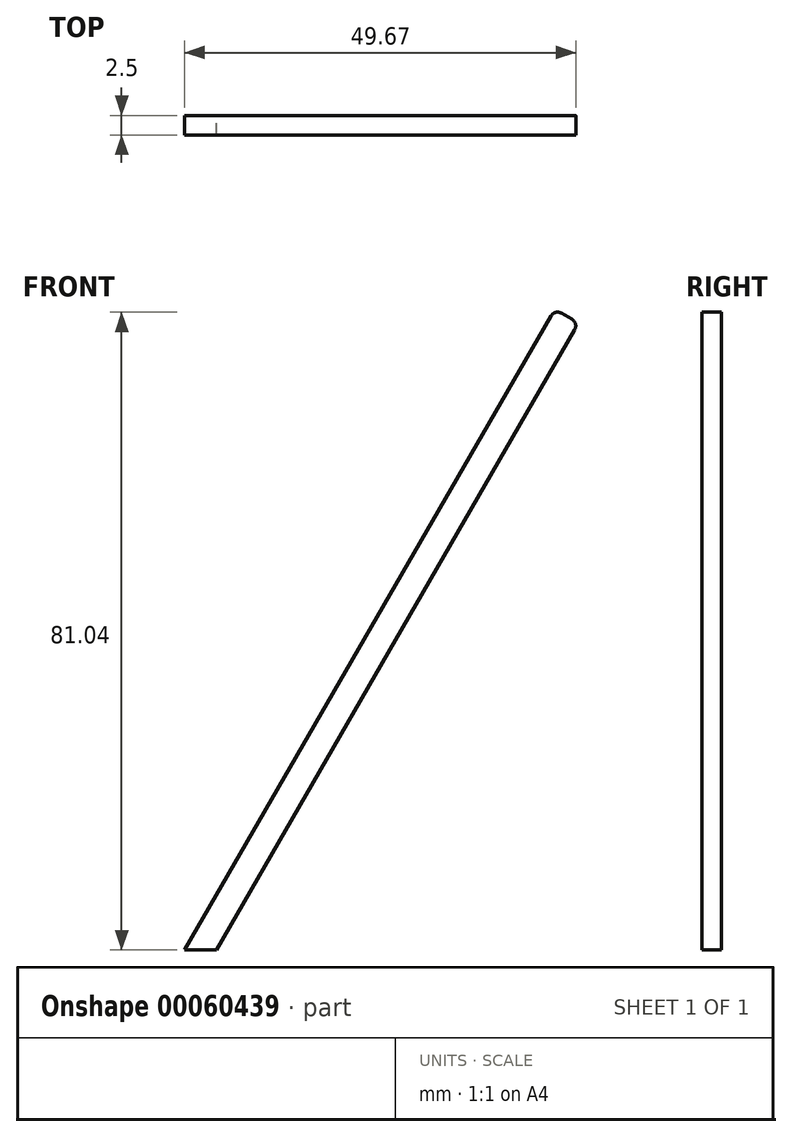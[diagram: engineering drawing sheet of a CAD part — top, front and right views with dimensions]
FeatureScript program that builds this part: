
annotation { "Feature Type Name" : "Feature", "Feature Type Description" : "" }
export const myFeature = defineFeature(function(context is Context, id is Id, definition is map)
    precondition{}
    {
        {
            var Q0;
            Q0=qCreatedBy(makeId("Front.planeOp"),FACE);
            var sketch = newSketch(context, id + "F0", { "sketchPlane" : qUnion([Q0])});
            skLineSegment(sketch, "E0.bottom", {"start": v(0, 0) * mm, "end": v(3.5, 0) * mm});
            skLineSegment(sketch, "E0.top", {"start": v(0, 94) * mm, "end": v(3.5, 94) * mm});
            skLineSegment(sketch, "E0.left", {"start": v(0, 0) * mm, "end": v(0, 94) * mm});
            skLineSegment(sketch, "E0.right", {"start": v(3.5, 0) * mm, "end": v(3.5, 94) * mm});
            skSolve(sketch);
        }
        {
            var Q0;
            Q0 = qSketchRegion(id + "F0", true);
            extrude(context, id + "F1", {"entities" : qUnion([Q0]), "depth" : 2.5 * mm});
        }
        {
            var Q0;
            Q0=makeQuery(id+"F1.opExtrude","SWEPT_EDGE",EDGE,{"disambiguationData":[OSD([sQuery(id+"F0.wireOp",EDGE,"E0.top"),sQuery(id+"F0.wireOp",EDGE,"E0.left")])]});
            var Q1;
            Q1=makeQuery(id+"F1.opExtrude","SWEPT_EDGE",EDGE,{"disambiguationData":[OSD([sQuery(id+"F0.wireOp",EDGE,"E0.top"),sQuery(id+"F0.wireOp",EDGE,"E0.right")])]});
            fillet(context, id + "F2", {"entities" : qUnion([Q0, Q1]), "radius" : 1 * mm, "allowEdgeOverflow" : false});
        }
        {
            var Q0;
            Q0=makeQuery(id+"F1.opExtrude","SWEPT_BODY",BODY,{"disambiguationData":[OSD([sQuery(id+"F0.wireOp",EDGE,"E0.bottom"),sQuery(id+"F0.wireOp",EDGE,"E0.top"),sQuery(id+"F0.wireOp",EDGE,"E0.left"),sQuery(id+"F0.wireOp",EDGE,"E0.right")])]});
            var Q1;
            Q1=makeQuery(id+"F1.opExtrude","SWEPT_EDGE",EDGE,{"disambiguationData":[OSD([sQuery(id+"F0.wireOp",EDGE,"E0.bottom"),sQuery(id+"F0.wireOp",EDGE,"E0.left")])]});
            transform(context, id + "F3", {"entities" : qUnion([Q0]), "transformType" : TransformType.ROTATION, "transformAxis" : qUnion([Q1]), "angle" : 30 * degree, "makeCopy" : false});
        }
        {
            var Q0;
            Q0=qCreatedBy(makeId("Front.planeOp"),FACE);
            var sketch = newSketch(context, id + "F4", { "sketchPlane" : qUnion([Q0])});
            skLineSegment(sketch, "E1.bottom", {"start": v(-30.77, 0) * mm, "end": v(32.26, 0) * mm});
            skLineSegment(sketch, "E1.top", {"start": v(-30.77, -8.78) * mm, "end": v(32.26, -8.78) * mm});
            skLineSegment(sketch, "E1.left", {"start": v(-30.77, 0) * mm, "end": v(-30.77, -8.78) * mm});
            skLineSegment(sketch, "E1.right", {"start": v(32.26, 0) * mm, "end": v(32.26, -8.78) * mm});
            skSolve(sketch);
        }
        {
            var Q0;
            Q0=makeQuery(id+"F4.imprint","IMPRINT",FACE,{"disambiguationData":[TD([[makeQuery(id+"F4.imprint","IMPRINT",EDGE,{"derivedFrom":sQuery(id+"F4.wireOp",EDGE,"E1.bottom")}),-1.0]])]});
            extrude(context, id + "F5", {"entities" : qUnion([Q0]), "depth" : 25 * mm});
        }
        {
            var Q0;
            Q0=makeQuery(id+"F5.opExtrude","SWEPT_BODY",BODY,{"disambiguationData":[OSD([sQuery(id+"F4.wireOp",EDGE,"E1.bottom"),sQuery(id+"F4.wireOp",EDGE,"E1.top"),sQuery(id+"F4.wireOp",EDGE,"E1.left"),sQuery(id+"F4.wireOp",EDGE,"E1.right")])]});
            var Q1;
            Q1=makeQuery(id+"F1.opExtrude","SWEPT_BODY",BODY,{"disambiguationData":[OSD([sQuery(id+"F0.wireOp",EDGE,"E0.bottom"),sQuery(id+"F0.wireOp",EDGE,"E0.top"),sQuery(id+"F0.wireOp",EDGE,"E0.left"),sQuery(id+"F0.wireOp",EDGE,"E0.right")])]});
            booleanBodies(context, id + "F6", {"operationType" : BooleanOperationType.SUBTRACTION, "tools" : qUnion([Q0]), "targets" : qUnion([Q1])});
        }
    });
